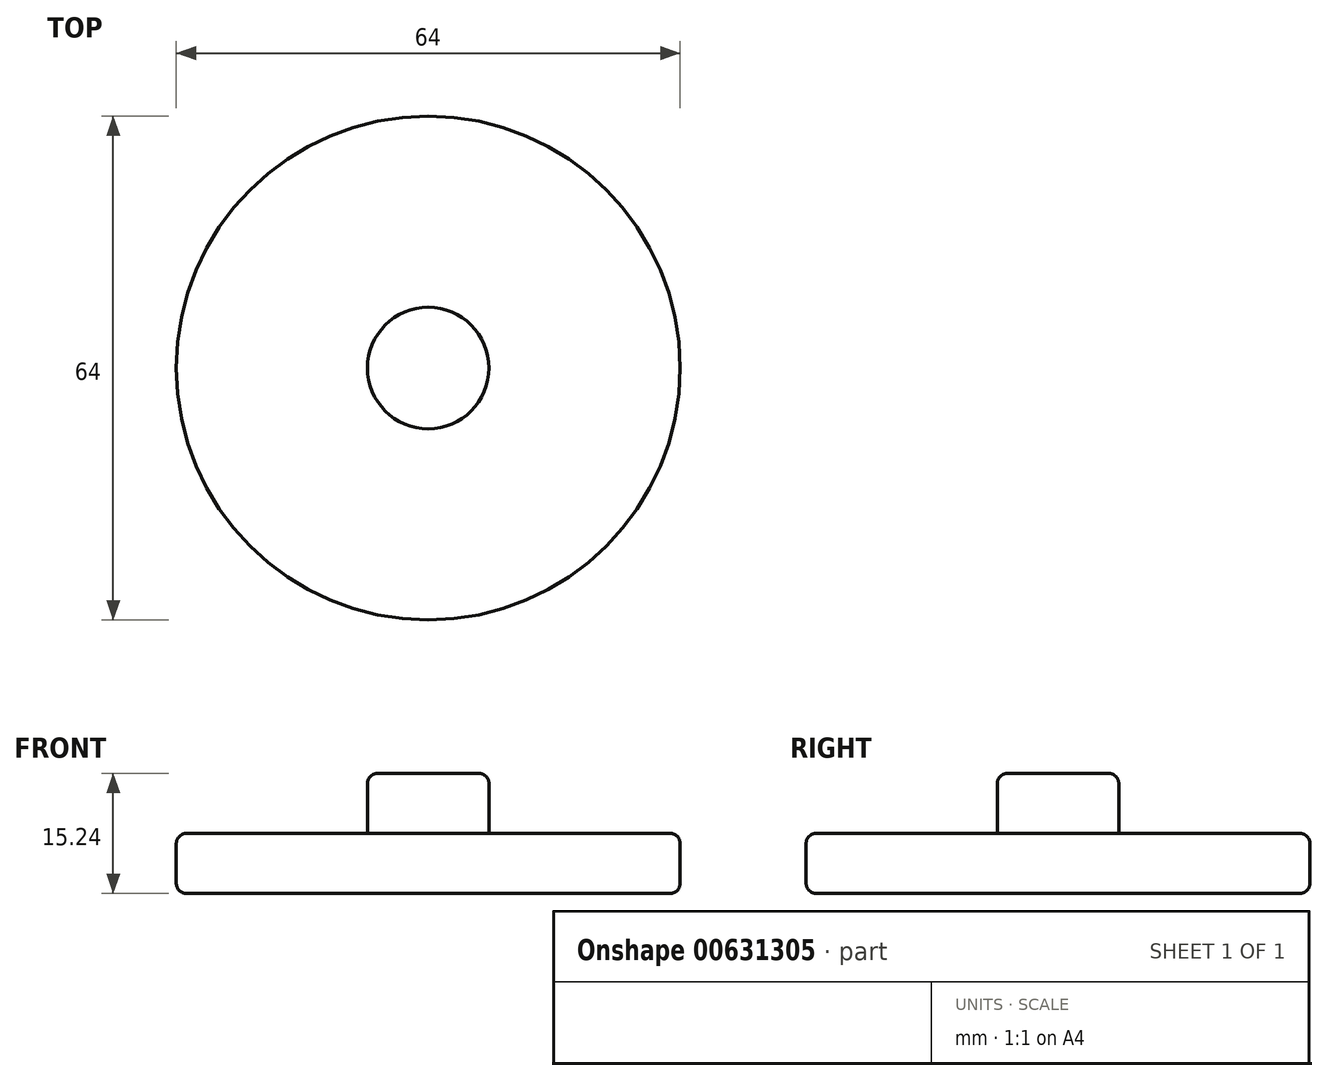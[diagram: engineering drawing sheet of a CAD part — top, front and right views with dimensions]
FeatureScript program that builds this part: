
annotation { "Feature Type Name" : "Feature", "Feature Type Description" : "" }
export const myFeature = defineFeature(function(context is Context, id is Id, definition is map)
    precondition{}
    {
        {
            var Q0;
            Q0=qCreatedBy(makeId("Top.planeOp"),FACE);
            var sketch = newSketch(context, id + "F0", { "sketchPlane" : qUnion([Q0])});
            skCircle(sketch, "E0", {"center": v(0, 0) * mm, "radius": 32 * mm});
            skSolve(sketch);
        }
        {
            var Q0;
            Q0=makeQuery(id+"F0.imprint","IMPRINT",FACE,{"disambiguationData":[TD([[makeQuery(id+"F0.imprint","IMPRINT",EDGE,{"derivedFrom":sQuery(id+"F0.wireOp",EDGE,"E0")}),1.0]])]});
            extrude(context, id + "F1", {"entities" : qUnion([Q0]), "depth" : 7.62 * mm, "offsetDistance" : 25.4 * mm});
        }
        {
            var Q0;
            Q0=makeQuery(id+"F1.opExtrude","CAP_FACE",FACE,{"disambiguationData":[OSD([sQuery(id+"F0.wireOp",EDGE,"E0")])],"isStart":false});
            var sketch = newSketch(context, id + "F2", { "sketchPlane" : qUnion([Q0])});
            skCircle(sketch, "E1", {"center": v(0, 0) * mm, "radius": 7.72 * mm});
            skSolve(sketch);
        }
        {
            var Q0;
            Q0=makeQuery(id+"F2.imprint","IMPRINT",FACE,{"disambiguationData":[TD([[makeQuery(id+"F2.imprint","IMPRINT",EDGE,{"derivedFrom":sQuery(id+"F2.wireOp",EDGE,"E1")}),1.0]])]});
            extrude(context, id + "F3", {"entities" : qUnion([Q0]), "operationType" : NewBodyOperationType.ADD, "depth" : 7.62 * mm, "offsetDistance" : 25.4 * mm});
        }
        {
            var Q0;
            Q0=makeQuery(id+"F3.opExtrude","CAP_EDGE",EDGE,{"disambiguationData":[OSD([sQuery(id+"F2.wireOp",EDGE,"E1")])],"isStart":false});
            var Q1;
            Q1=makeQuery(id+"F1.opExtrude","CAP_EDGE",EDGE,{"disambiguationData":[OSD([sQuery(id+"F0.wireOp",EDGE,"E0")])],"isStart":false});
            var Q2;
            Q2=makeQuery(id+"F3.opExtrude","CAP_EDGE",EDGE,{"disambiguationData":[OSD([sQuery(id+"F2.wireOp",EDGE,"E1")])],"isStart":true});
            var Q3;
            Q3=makeQuery(id+"F1.opExtrude","CAP_EDGE",EDGE,{"disambiguationData":[OSD([sQuery(id+"F0.wireOp",EDGE,"E0")])],"isStart":true});
            fillet(context, id + "F4", {"entities" : qUnion([Q0, Q1, Q2, Q3]), "radius" : 1.27 * mm, "tangentPropagation" : true, "allowEdgeOverflow" : false});
        }
    });
